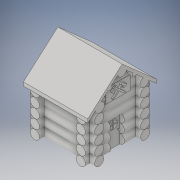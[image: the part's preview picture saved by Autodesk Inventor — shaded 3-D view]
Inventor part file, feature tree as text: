
AUTODESK INVENTOR PART (.ipt)
format: ipt  version: 2018 (Build 220112000, 112)  size: 829,440 bytes
history: native  units: in
note: dims shown in document units (in); Inventor stores cm internally (conversion verified against a paired STEP export)
features: extrude x14, sketch x14, plane x5, mirror x5, projected_geometry x2, fillet x1
ambient origin geometry x8: Origin, YZ Plane, XZ Plane, XY Plane, X Axis, Y Axis, Z Axis, Center Point
bodies: Solid1 (feature_tree)
feature tree (41):
  extrude  "Extrusion1"  Depth=2.5in
  extrude  "Extrusion2"  Depth=0.5in
  extrude  "Extrusion3"  Depth=0.25in
  sketch  "Sketch4"  dims[d7=0.5in d8=0.5in]
  plane  "Work Plane1"
  mirror  "Mirror1"
  plane  "Work Plane4"
  extrude  "Extrusion4"  Depth=0.5in
  mirror  "Mirror2"
  mirror  "Mirror3"
  extrude  "Extrusion5"  Depth=0.25in
  sketch  "Sketch8"  dims[d13=0.25in d14=4.0in d15=0.0in]
  extrude  "Extrusion6"  Depth=0.25in
  extrude  "Extrusion7"  Depth=0.25in TaperAngle=0.0deg
  extrude  "Extrusion8"  Depth=0.25in
  mirror  "Mirror4"
  plane  "Work Plane5"
  mirror  "Mirror5"
  plane  "Work Plane6"
  extrude  "Extrusion9"  Depth=1.75in
  extrude  "Extrusion10"  Depth=0.25in
  extrude  "Extrusion11"  Depth=0.25in
  extrude  "Extrusion12"  Depth=0.25in
  extrude  "Extrusion13"  Depth=0.25in TaperAngle=0.0deg
  extrude  "Extrusion14"  Depth=0.15in
  fillet  "Fillet1"  Radius=0.15in
  sketch  "Sketch1"  dims[d0=3.0in d1=2.5in]
  sketch  "Sketch2"  dims[d2=3.5in d3=0.0in d4=0.5in]
  sketch  "Sketch3"  dims[d5=90.0deg d6=0.25in]
  projected_geometry  "Projected Loop1"
  plane  "Work Plane3"
  sketch  "Sketch5"  dims[d9=0.5in d10=0.25in]
  sketch  "Sketch6"  dims[d11=0.25in d12=0.25in]
  projected_geometry  "Projected Loop2"
  sketch  "Sketch9"  dims[d16=0.25in d17=0.25in]
  sketch  "Sketch10"  dims[d18=0.5in d19=0.0in d20=1.75in]
  sketch  "Sketch11"  dims[d21=0.25in d22=0.25in]
  sketch  "Sketch12"  dims[d23=0.5in d24=0.25in]
  sketch  "Sketch13"  dims[d25=0.25in d26=0.25in]
  sketch  "Sketch14"  dims[d27=0.25in d28=3.5in d29=0.0in]
  sketch  "Sketch15"  dims[d30=0.15in d31=0.15in d32=0.15in d33=0.15in d34=0.5in d35=1.1in d36=1.1in d37=2.05in d38=0.0in d39=0.125in d40=0.125in d42=0.0in d43=0.2in d44=0.2in d45=0.15in d46=0.5in d47=0.136in d48=0.5in d49=0.0in d50=0.34in d51=0.25in d53=1.2in d54=3.5in d55=0.0in d56=3.5in d57=0.0in d58=0.5in d59=0.25in d60=0.5in d61=0.25in d64=0.168in d65=0.168in d66=0.1684in d67=0.25in d68=0.0in d69=1.0in d70=0.0in d71=0.25in d72=-0.225in d73=1.2in d74=1.2in d75=0.85in d76=0.75in d77=1.0in d78=0.0in d79=0.075in d80=0.0375in d81=0.35in d82=0.12in d83=0.15in d84=0.2in d85=0.125in d86=0.3779in d87=0.8921in d88=0.56in d89=0.0in d90=0.0in d91=0.0375in d92=0.575in d93=0.0625in d94=0.0in d96=1.375in d97=1.5in d98=0.75in d99=0.275in d100=0.0in d101=0.5in d102=0.05in d103=0.025in d104=0.375in d105=0.025in d106=0.025in d107=0.4in d108=0.3in d109=0.0in d110=0.08in d111=0.75in d112=0.1in d113=0.1in d114=0.0in d115=0.11in d116=0.07in d117=0.0in d118=0.04in]
